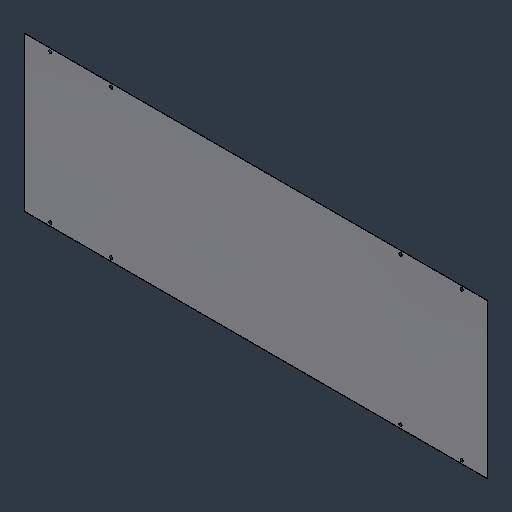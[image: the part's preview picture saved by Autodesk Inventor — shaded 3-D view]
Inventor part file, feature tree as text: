
AUTODESK INVENTOR PART (.ipt)
format: ipt  version: 2024.3 (Build 283343000, 343)  size: 85,504 bytes
history: native  units: mm (DEFAULTED — no unit token found)
features: mirror x1
ambient origin geometry x8: Origin, YZ Plane, XZ Plane, XY Plane, X Axis, Y Axis, Z Axis, Center Point
bodies: Solid1 (feature_tree)
feature tree (1):
  mirror  "Mirror1"
